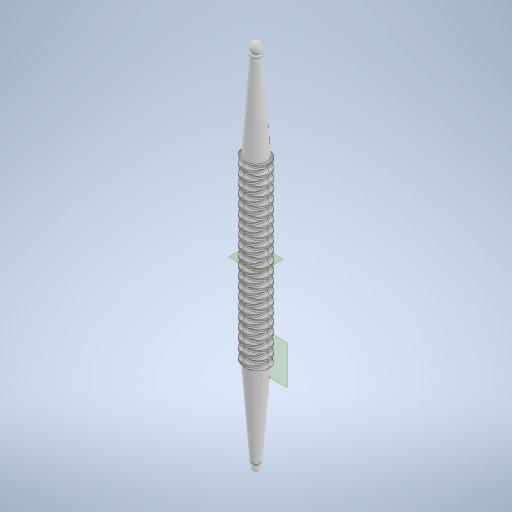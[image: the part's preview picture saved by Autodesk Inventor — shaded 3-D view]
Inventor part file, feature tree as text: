
AUTODESK INVENTOR PART (.ipt)
format: ipt  version: 2024 (Build 280153000, 153)  size: 3,283,968 bytes
history: native  units: mm
features: sketch x13, chamfer x10, extrude x5, helix x4, revolve x3, plane x2, fillet x2
ambient origin geometry x8: Origin, YZ Plane, XZ Plane, XY Plane, X Axis, Y Axis, Z Axis, Center Point
bodies: Solid1 (feature_tree)
feature tree (39):
  extrude  "Extrusion1"  Depth=2.0mm TaperAngle=0.0deg
  helix  "Coil1"  [1 undecoded]
  helix  "Coil2"  [1 undecoded]
  helix  "Coil3"  [1 undecoded]
  helix  "Coil4"  [1 undecoded]
  chamfer  "Chamfer1"  Distance=2.0mm Angle=45.0deg
  chamfer  "Chamfer2"  Distance=2.0mm Angle=45.0deg
  chamfer  "Chamfer3"  Distance=2.0mm Angle=45.0deg
  chamfer  "Chamfer4"  Distance=2.0mm Angle=45.0deg
  chamfer  "Chamfer5"  Distance=2.0mm Angle=45.0deg
  chamfer  "Chamfer6"  Distance=2.0mm Angle=45.0deg
  chamfer  "Chamfer7"  Distance=2.0mm Angle=45.0deg
  chamfer  "Chamfer8"  Distance=50.0mm
  extrude  "Extrusion2"  [1 undecoded]
  chamfer  "Chamfer9"  Distance=50.0mm
  plane  "Work Plane4"
  extrude  "Extrusion3"  Depth=4.0mm
  chamfer  "Chamfer10"  Angle=90.0deg  [1 undecoded]
  revolve  "Revolution3"  [1 undecoded]
  revolve  "Revolution4"  [1 undecoded]
  fillet  "Fillet1"  Radius=1.0mm
  revolve  "Revolution5"  [1 undecoded]
  fillet  "Fillet2"  Radius=1.0mm
  sketch  "Sketch22"  dims[d81=5.0mm]
  plane  "Work Plane6"
  sketch  "Sketch23"  dims[d82=90.0deg]
  extrude  "Extrusion4"  Depth=2.0mm
  extrude  "Extrusion5"  Depth=2.0mm TaperAngle=0.0deg
  sketch  "Sketch1"  dims[d0=15.0mm d1=100.0mm d2=0.0mm d3=2.0mm]
  sketch  "Sketch2"  dims[d4=10.0mm d5=10.0mm d6=100.0mm d7=0.0mm d8=90.0deg d9=90.0deg d10=0.0mm d11=0.0mm]
  sketch  "Sketch4"  dims[d12=10.0mm d13=10.0mm d14=100.0mm d15=0.0mm d16=90.0deg d17=90.0deg d18=0.0mm d19=0.0mm d20=2.0mm]
  sketch  "Sketch5"  dims[d21=10.0mm d22=10.0mm d23=100.0mm d24=0.0mm d25=90.0deg d26=90.0deg d27=0.0mm d28=0.0mm d29=2.0mm]
  sketch  "Sketch6"  dims[d30=10.0mm d31=10.0mm d32=100.0mm d33=0.0mm d34=90.0deg d35=90.0deg d36=0.0mm d37=0.0mm d38=1.0mm d39=2.0mm d40=45.0deg d41=1.0mm d42=2.0mm d43=45.0deg d44=1.0mm d45=2.0mm d46=45.0deg d47=1.0mm d48=2.0mm d49=45.0deg d50=1.0mm d51=2.0mm d52=45.0deg d53=1.0mm d54=2.0mm d55=45.0deg d56=1.0mm d57=2.0mm d58=45.0deg d59=1.0mm d60=2.0mm d61=45.0deg]
  sketch  "Sketch8"  dims[d62=12.0mm d63=50.0mm d64=0.0mm]
  sketch  "Sketch11"  dims[d65=50.0mm d66=50.0mm d67=0.698132mm d69=-50.0mm]
  sketch  "Sketch15"  dims[d71=12.0mm d72=50.0mm d73=0.0mm]
  sketch  "Sketch16"  dims[d74=50.0mm d75=50.0mm d76=0.698132mm d79=4.0mm]
  sketch  "Sketch18"  dims[d80=90.0deg]
  sketch  "Sketch24"  dims[d83=2.0mm d87=90.0deg d88=2.0mm d97=8.0mm d98=1.0mm d99=1.0mm d100=1.0mm d101=1.0mm d102=3.0mm d103=0.0mm d104=5.0mm d106=8.0mm d107=1.0mm d108=3.0mm d109=0.0mm d110=1.0mm d111=1.0mm d112=1.0mm]
note: 9 required parameter values undecoded (feature->parameter linkage not recoverable at this tier; creation-order binding heuristic only, values carry confidence <= 0.55)